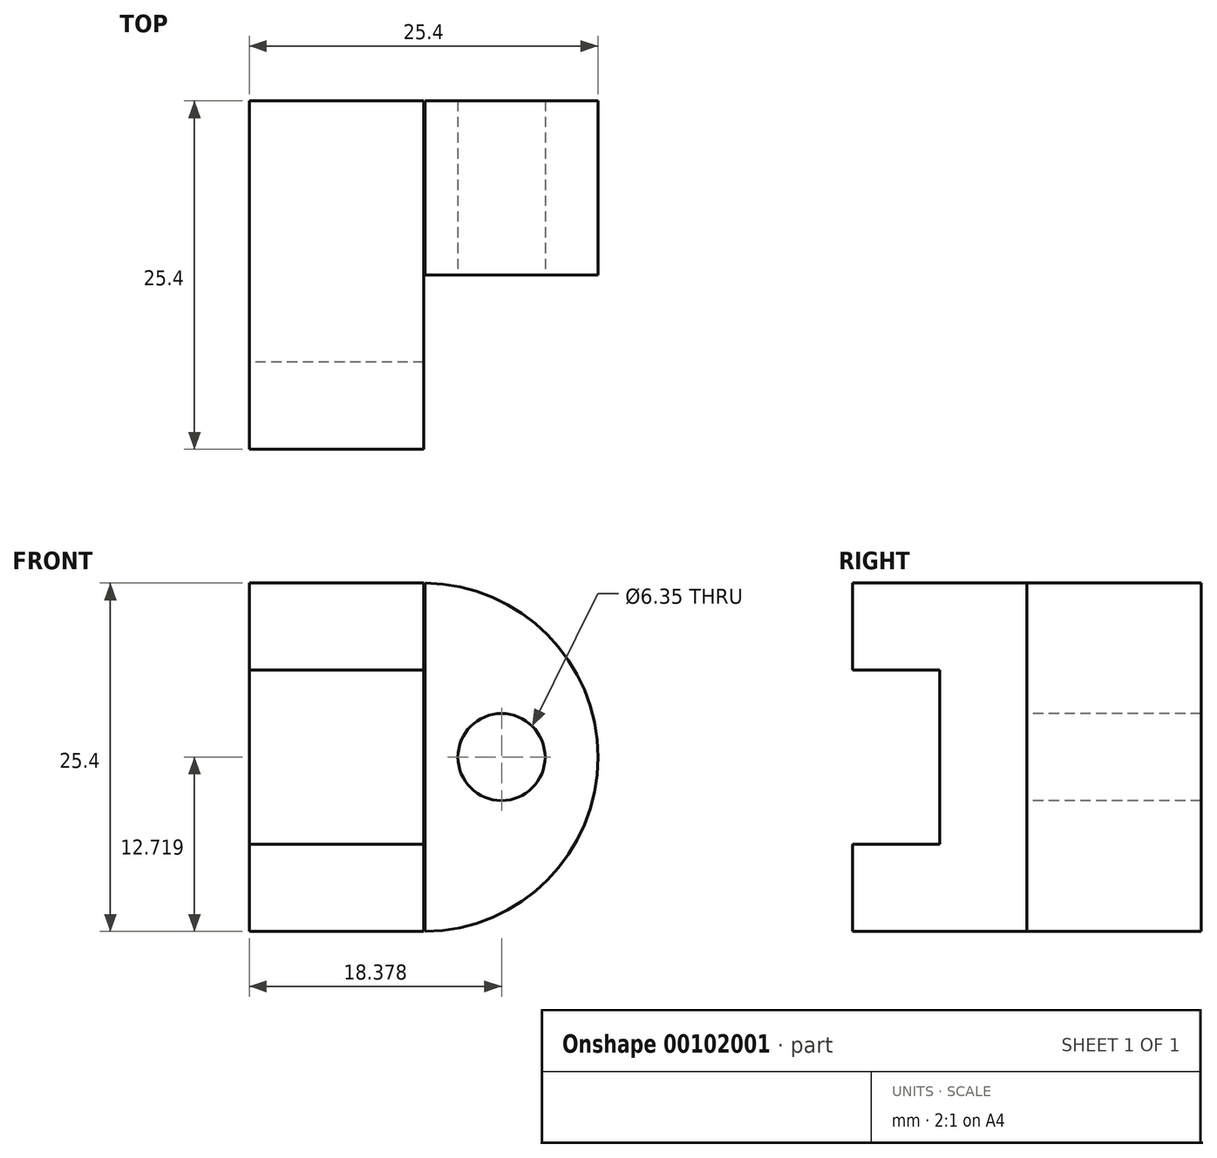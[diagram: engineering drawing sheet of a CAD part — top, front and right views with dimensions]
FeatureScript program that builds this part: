
annotation { "Feature Type Name" : "Feature", "Feature Type Description" : "" }
export const myFeature = defineFeature(function(context is Context, id is Id, definition is map)
    precondition{}
    {
        {
            var Q0;
            Q0=qCreatedBy(makeId("Right.planeOp"),FACE);
            var sketch = newSketch(context, id + "F0", { "sketchPlane" : qUnion([Q0])});
            skLineSegment(sketch, "E0", {"start": v(0, 0) * mm, "end": v(0, 25.4) * mm});
            skLineSegment(sketch, "E1", {"start": v(0, 25.4) * mm, "end": v(-25.4, 25.4) * mm});
            skLineSegment(sketch, "E2", {"start": v(-25.4, 25.4) * mm, "end": v(-25.4, 19.05) * mm});
            skLineSegment(sketch, "E3", {"start": v(-25.4, 19.05) * mm, "end": v(-19.05, 19.05) * mm});
            skLineSegment(sketch, "E4", {"start": v(-19.05, 19.05) * mm, "end": v(-19.05, 6.35) * mm});
            skLineSegment(sketch, "E5", {"start": v(-19.05, 6.35) * mm, "end": v(-25.4, 6.35) * mm});
            skLineSegment(sketch, "E6", {"start": v(-25.4, 6.35) * mm, "end": v(-25.4, 0) * mm});
            skLineSegment(sketch, "E7", {"start": v(-25.4, 0) * mm, "end": v(0, 0) * mm});
            skSolve(sketch);
        }
        {
            var Q0;
            Q0 = qSketchRegion(id + "F0", true);
            extrude(context, id + "F1", {"entities" : qUnion([Q0]), "depth" : 12.7 * mm});
        }
        {
            var Q0;
            Q0=qCreatedBy(makeId("Front.planeOp"),FACE);
            var sketch = newSketch(context, id + "F2", { "sketchPlane" : qUnion([Q0])});
            skArc(sketch, "E8", {"start": v(12.8, 0) * mm, "mid": v(25.4, 12.7) * mm, "end": v(12.8, 25.4) * mm});
            skLineSegment(sketch, "E9", {"start": v(12.8, 0) * mm, "end": v(12.8, 25.4) * mm});
            skSolve(sketch);
        }
        {
            var Q0;
            Q0 = qSketchRegion(id + "F2", true);
            extrude(context, id + "F3", {"entities" : qUnion([Q0]), "depth" : 12.7 * mm});
        }
        {
            var Q0;
            Q0=makeQuery(id+"F3.opExtrude","CAP_FACE",FACE,{"disambiguationData":[OSD([sQuery(id+"F2.wireOp",EDGE,"E8"),sQuery(id+"F2.wireOp",EDGE,"E9")])],"isStart":false});
            var sketch = newSketch(context, id + "F4", { "sketchPlane" : qUnion([Q0])});
            skCircle(sketch, "E10", {"center": v(18.38, 12.72) * mm, "radius": 3.18 * mm});
            skSolve(sketch);
        }
        {
            var Q0;
            Q0 = qSketchRegion(id + "F4", true);
            extrude(context, id + "F5", {"entities" : qUnion([Q0]), "operationType" : NewBodyOperationType.REMOVE, "endBound" : BoundingType.THROUGH_ALL, "oppositeDirection" : true, "depth" : 25.4 * mm});
        }
    });
